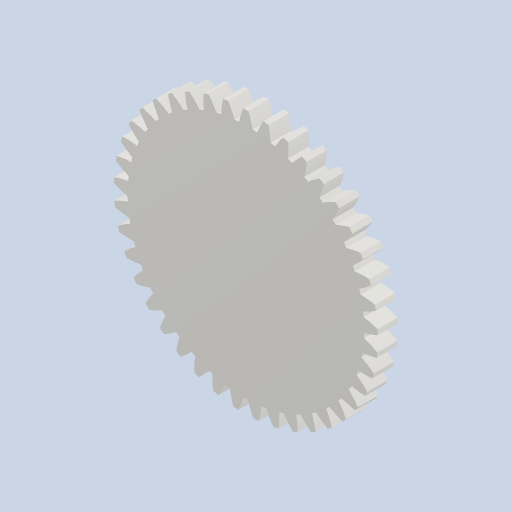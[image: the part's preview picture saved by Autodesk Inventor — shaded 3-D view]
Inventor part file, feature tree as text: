
AUTODESK INVENTOR PART (.ipt)
format: ipt  version: 2022 (Build 260153000, 153)  size: 306,176 bytes
history: native  units: mm (DEFAULTED — no unit token found)
features: plane x3, other x3, sketch x2, extrude x1
ambient origin geometry x8: Origin, YZ Plane, XZ Plane, XY Plane, X Axis, Y Axis, Z Axis, Center Point
bodies: Solid1 (feature_tree)
feature tree (9):
  extrude  "Extrusion1"  Depth=5.0mm TaperAngle=0.0deg
  plane  "Work Plane2"
  plane  "Work Plane8"
  plane  "Work Plane9"
  other  "Цилиндрическое зубчатое зацепление"
  sketch  "Sketch1"  dims[d0=65.033866mm d1=5.0mm d2=0.0mm]
  sketch  "Sketch2"  dims[d3=61.5mm d4=10.0mm d5=0.0mm d16=38.516933mm d17=0.0mm d34=0.766242mm d39=0.0mm d41=0.0mm d43=38.516933mm d46=38.516933mm d47=0.0mm d48=0.0mm]
  other  "Srf1"
  other  "Средний диаметр"
